# Revit family: 205_SIL-50-_-900
name_source: partatom
category: Duct Accessories
units: mm (PartAtom-declared; Revit-internal decimal feet)

## family parameters
Always vertical = Yes
Cut with Voids When Loaded = No
Part Type = Breaks Into
Round Connector Dimension = Use Diameter
Shared = No
Work Plane-Based = No

## types (15) — shared parameters
Description = CIRCULAR SILENCER
L2D = 900 mm
LL = 450 mm  [stored 1.47638 ft]
Manufacturer = Alnor
QmdConnectorList = 201;D;202;D
URL = http://www.ventilation-alnor.co.uk
magiPartTypeId = 205
magiProductFamilyId = SIL-50-*-900

## per-type parameters (varying)
| type | CD1 | CD2 | D | H2D | L1 | L2 | R | SW1 | W2D |
| SIL-50-080-900 | 90 mm  [stored 0.295276 ft] | 91 mm  [stored 0.298556 ft] | 80 mm | 180 mm  [stored 0.590551 ft] | 4 mm  [stored 0.0131234 ft] | 892 mm | 40 mm  [stored 0.131234 ft] | Yes | 180 mm  [stored 0.590551 ft] |
| SIL-50-630-900 | 355 mm | 356 mm | 630 mm | 730 mm | 4 mm  [stored 0.0131234 ft] | 892 mm | 315 mm | Yes | 730 mm |
| SIL-50-560-900 | 315 mm | 316 mm | 560 mm | 660 mm | 4 mm  [stored 0.0131234 ft] | 892 mm | 280 mm | Yes | 660 mm |
| SIL-50-500-900 | 300 mm | 301 mm | 500 mm | 600 mm | 4 mm  [stored 0.0131234 ft] | 892 mm | 250 mm | Yes | 600 mm |
| SIL-50-450-900 | 280 mm | 281 mm | 450 mm | 550 mm | 4 mm  [stored 0.0131234 ft] | 892 mm | 225 mm  [stored 0.738189 ft] | Yes | 550 mm |
| SIL-50-400-900 | 250 mm | 251 mm | 400 mm | 500 mm | 4 mm  [stored 0.0131234 ft] | 892 mm | 200 mm | Yes | 500 mm |
| SIL-50-355-900 | 225 mm  [stored 0.738189 ft] | 226 mm | 355 mm | 455 mm | 4 mm  [stored 0.0131234 ft] | 892 mm | 178 mm | Yes | 455 mm |
| SIL-50-315-900 | 200 mm | 201 mm | 315 mm | 415 mm | 4 mm  [stored 0.0131234 ft] | 892 mm | 158 mm | Yes | 415 mm |
| SIL-50-300-900 | 200 mm | 201 mm | 300 mm | 400 mm | 4 mm  [stored 0.0131234 ft] | 892 mm | 150 mm | Yes | 400 mm |
| SIL-50-250-900 | 178 mm | 179 mm | 250 mm | 350 mm | 36 mm | 828 mm | 125 mm | No | 350 mm |
| SIL-50-200-900 | 150 mm | 151 mm | 200 mm | 300 mm | 36 mm | 828 mm | 100 mm  [stored 0.328084 ft] | No | 300 mm |
| SIL-50-160-900 | 125 mm | 126 mm | 160 mm | 260 mm | 36 mm | 828 mm | 80 mm  [stored 0.262467 ft] | No | 260 mm |
| SIL-50-150-900 | 125 mm | 126 mm | 150 mm | 250 mm | 4 mm  [stored 0.0131234 ft] | 892 mm | 75 mm | Yes | 250 mm |
| SIL-50-125-900 | 112 mm | 113 mm | 125 mm | 225 mm  [stored 0.738189 ft] | 36 mm | 828 mm | 63 mm | No | 225 mm  [stored 0.738189 ft] |
| SIL-50-100-900 | 100 mm  [stored 0.328084 ft] | 101 mm | 100 mm | 200 mm | 36 mm | 828 mm | 50 mm | No | 200 mm |

note: column(s) folded — value = type name in every type: MC Product Code, magiProductId

note: [stored X ft] marks values corroborated as IEEE doubles in the binary element streams (Revit-internal decimal feet)

## geometry (parser evidence)
native form markers: Blend x4, Sweep x1
no freeform markers — native parametric forms only
